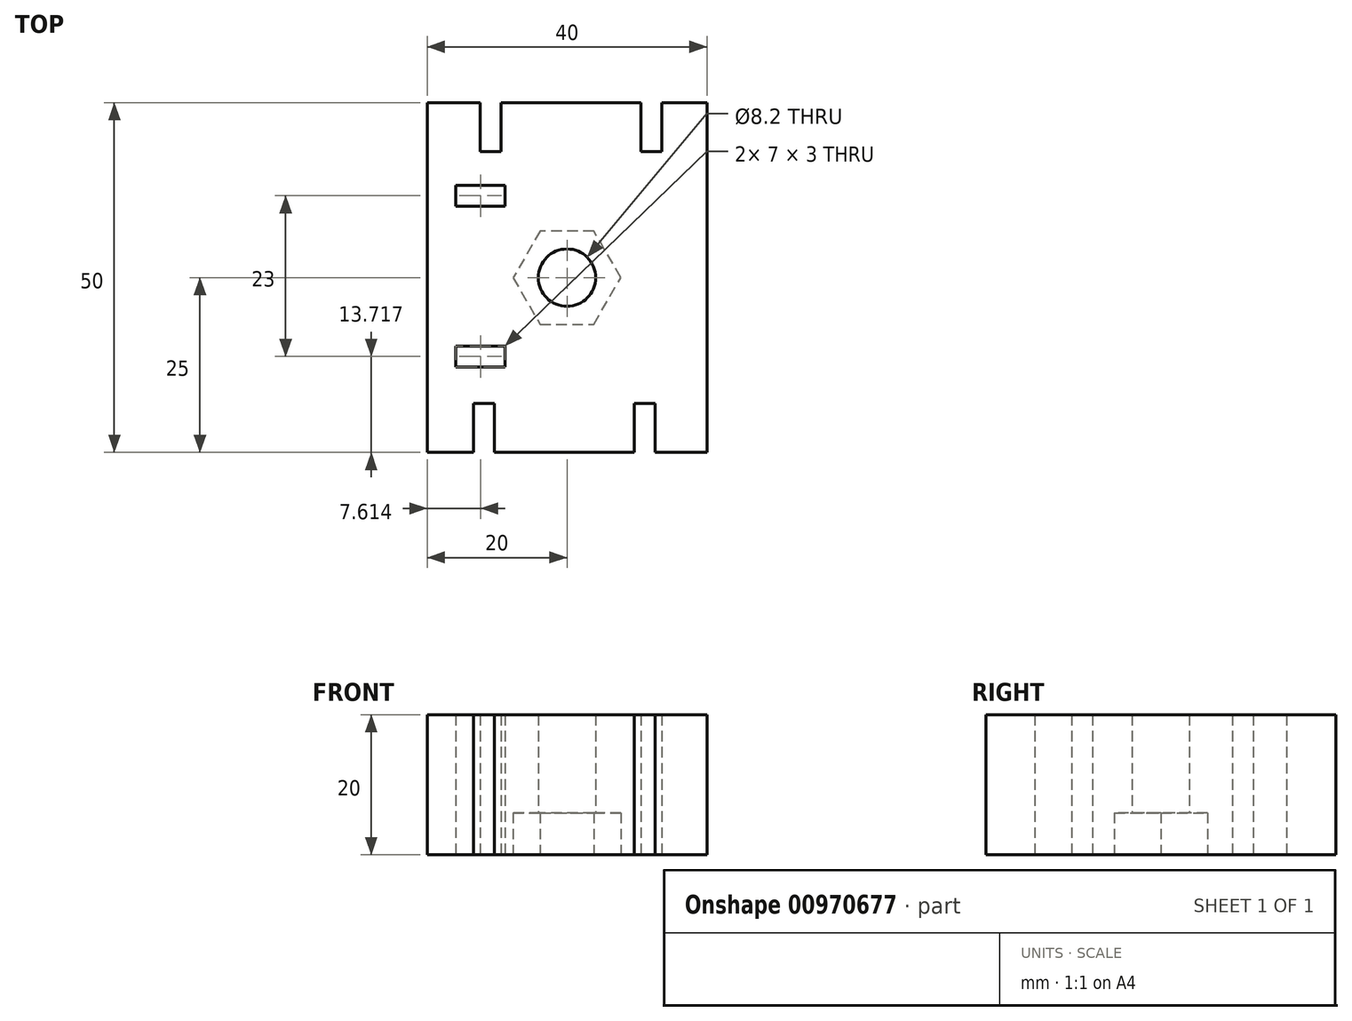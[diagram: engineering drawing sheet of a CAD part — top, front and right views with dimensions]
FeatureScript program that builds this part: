
annotation { "Feature Type Name" : "Feature", "Feature Type Description" : "" }
export const myFeature = defineFeature(function(context is Context, id is Id, definition is map)
    precondition{}
    {
        {
            var Q0;
            Q0=qCreatedBy(makeId("Top.planeOp"),FACE);
            var sketch = newSketch(context, id + "F0", { "sketchPlane" : qUnion([Q0])});
            skLineSegment(sketch, "E0.bottom", {"start": v(20, -25) * mm, "end": v(-20, -25) * mm});
            skLineSegment(sketch, "E0.top", {"start": v(20, 25) * mm, "end": v(-20, 25) * mm});
            skLineSegment(sketch, "E0.left", {"start": v(20, -25) * mm, "end": v(20, 25) * mm});
            skLineSegment(sketch, "E0.right", {"start": v(-20, -25) * mm, "end": v(-20, 25) * mm});
            skPoint(sketch, "E0.middle", {"position": v(0, 0) * mm});
            skCircle(sketch, "E1", {"center": v(0, 0) * mm, "radius": 4.1 * mm});
            skLineSegment(sketch, "E2.bottom", {"start": v(-15.89, 10.22) * mm, "end": v(-8.89, 10.22) * mm});
            skLineSegment(sketch, "E2.top", {"start": v(-15.89, 13.22) * mm, "end": v(-8.89, 13.22) * mm});
            skLineSegment(sketch, "E2.left", {"start": v(-15.89, 10.22) * mm, "end": v(-15.89, 13.22) * mm});
            skLineSegment(sketch, "E2.right", {"start": v(-8.89, 10.22) * mm, "end": v(-8.89, 13.22) * mm});
            skPoint(sketch, "E2.middle", {"position": v(-12.39, 0) * mm});
            skLineSegment(sketch, "E3.bottom", {"start": v(-15.89, -12.78) * mm, "end": v(-8.89, -12.78) * mm});
            skLineSegment(sketch, "E3.top", {"start": v(-15.89, -9.78) * mm, "end": v(-8.89, -9.78) * mm});
            skLineSegment(sketch, "E3.left", {"start": v(-15.89, -12.78) * mm, "end": v(-15.89, -9.78) * mm});
            skLineSegment(sketch, "E3.right", {"start": v(-8.89, -12.78) * mm, "end": v(-8.89, -9.78) * mm});
            skLineSegment(sketch, "E4.bottom", {"start": v(-9.43, 25) * mm, "end": v(-12.43, 25) * mm});
            skLineSegment(sketch, "E4.top", {"start": v(-9.43, 18) * mm, "end": v(-12.43, 18) * mm});
            skLineSegment(sketch, "E4.left", {"start": v(-9.43, 25) * mm, "end": v(-9.43, 18) * mm});
            skLineSegment(sketch, "E4.right", {"start": v(-12.43, 25) * mm, "end": v(-12.43, 18) * mm});
            skLineSegment(sketch, "E5.bottom", {"start": v(10.57, 25) * mm, "end": v(13.57, 25) * mm});
            skLineSegment(sketch, "E5.top", {"start": v(10.57, 18) * mm, "end": v(13.57, 18) * mm});
            skLineSegment(sketch, "E5.left", {"start": v(10.57, 25) * mm, "end": v(10.57, 18) * mm});
            skLineSegment(sketch, "E5.right", {"start": v(13.57, 25) * mm, "end": v(13.57, 18) * mm});
            skLineSegment(sketch, "E6.bottom", {"start": v(-13.38, -25) * mm, "end": v(-10.38, -25) * mm});
            skLineSegment(sketch, "E6.top", {"start": v(-13.38, -18) * mm, "end": v(-10.38, -18) * mm});
            skLineSegment(sketch, "E6.left", {"start": v(-13.38, -25) * mm, "end": v(-13.38, -18) * mm});
            skLineSegment(sketch, "E6.right", {"start": v(-10.38, -25) * mm, "end": v(-10.38, -18) * mm});
            skLineSegment(sketch, "E7.bottom", {"start": v(9.62, -25) * mm, "end": v(12.62, -25) * mm});
            skLineSegment(sketch, "E7.top", {"start": v(9.62, -18) * mm, "end": v(12.62, -18) * mm});
            skLineSegment(sketch, "E7.left", {"start": v(9.62, -25) * mm, "end": v(9.62, -18) * mm});
            skLineSegment(sketch, "E7.right", {"start": v(12.62, -25) * mm, "end": v(12.62, -18) * mm});
            skSolve(sketch);
        }
        {
            var Q0;
            Q0=makeQuery(id+"F0.imprint","IMPRINT",FACE,{"disambiguationData":[TD([[makeQuery(id+"F0.imprint","IMPRINT",EDGE,{"derivedFrom":sQuery(id+"F0.wireOp",EDGE,"E0.bottom")}),-1.0]])]});
            extrude(context, id + "F1", {"entities" : qUnion([Q0]), "depth" : 20 * mm, "offsetDistance" : 25 * mm});
        }
        {
            var Q0;
            Q0=makeQuery(id+"F1.opExtrude","CAP_FACE",FACE,{"disambiguationData":[OSD([sQuery(id+"F0.wireOp",EDGE,"E0.bottom"),sQuery(id+"F0.wireOp",EDGE,"E0.top"),sQuery(id+"F0.wireOp",EDGE,"E0.left"),sQuery(id+"F0.wireOp",EDGE,"E0.right"),sQuery(id+"F0.wireOp",EDGE,"E1"),sQuery(id+"F0.wireOp",EDGE,"E2.bottom"),sQuery(id+"F0.wireOp",EDGE,"E2.top"),sQuery(id+"F0.wireOp",EDGE,"E2.left"),sQuery(id+"F0.wireOp",EDGE,"E2.right"),sQuery(id+"F0.wireOp",EDGE,"E3.bottom"),sQuery(id+"F0.wireOp",EDGE,"E3.top"),sQuery(id+"F0.wireOp",EDGE,"E3.left"),sQuery(id+"F0.wireOp",EDGE,"E3.right")])],"isStart":true});
            var sketch = newSketch(context, id + "F2", { "sketchPlane" : qUnion([Q0])});
            skCircle(sketch, "E8.cCircle", {"center": v(0, 0) * mm, "radius": 6.67 * mm, "construction": true});
            skLineSegment(sketch, "E8.0", {"start": v(7.7, -0.01) * mm, "end": v(3.84, -6.67) * mm});
            skLineSegment(sketch, "E8.1", {"start": v(3.84, -6.67) * mm, "end": v(-3.86, -6.66) * mm});
            skLineSegment(sketch, "E8.2", {"start": v(-3.86, -6.66) * mm, "end": v(-7.7, 0.01) * mm});
            skLineSegment(sketch, "E8.3", {"start": v(-7.7, 0.01) * mm, "end": v(-3.84, 6.67) * mm});
            skLineSegment(sketch, "E8.4", {"start": v(-3.84, 6.67) * mm, "end": v(3.86, 6.66) * mm});
            skLineSegment(sketch, "E8.5", {"start": v(3.86, 6.66) * mm, "end": v(7.7, -0.01) * mm});
            skPoint(sketch, "E8.0.midPoint", {"position": v(5.77, -3.34) * mm});
            skSolve(sketch);
        }
        {
            var Q0;
            Q0 = qSketchRegion(id + "F2", true);
            extrude(context, id + "F3", {"entities" : qUnion([Q0]), "operationType" : NewBodyOperationType.REMOVE, "oppositeDirection" : true, "depth" : 6 * mm, "offsetDistance" : 25 * mm});
        }
    });
